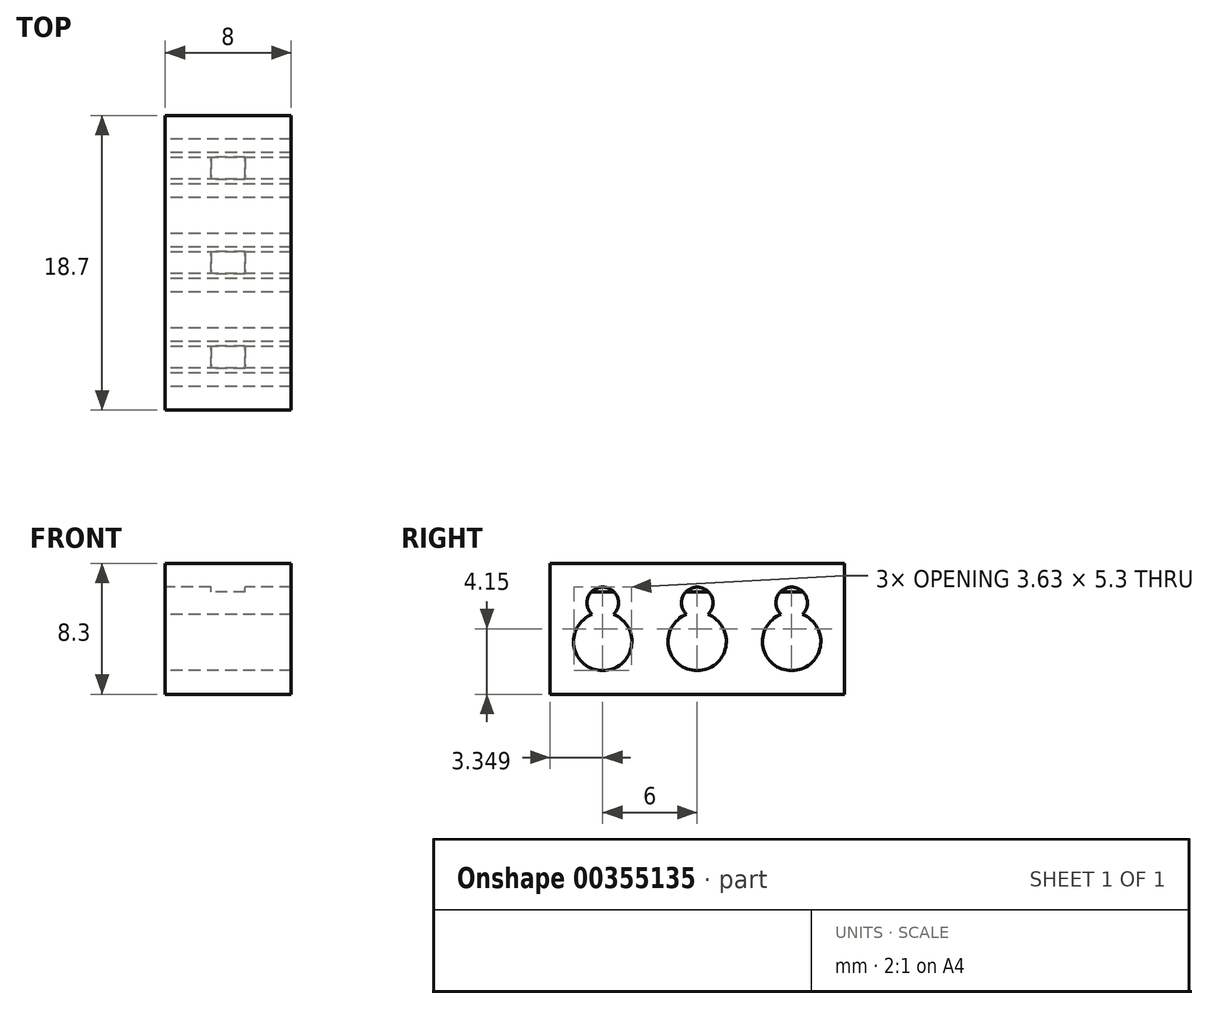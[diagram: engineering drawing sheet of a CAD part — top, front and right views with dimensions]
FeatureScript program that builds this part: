
annotation { "Feature Type Name" : "Feature", "Feature Type Description" : "" }
export const myFeature = defineFeature(function(context is Context, id is Id, definition is map)
    precondition{}
    {
        {
            var Q0;
            Q0=qCreatedBy(makeId("Right.planeOp"),FACE);
            var sketch = newSketch(context, id + "F0", { "sketchPlane" : qUnion([Q0])});
            skLineSegment(sketch, "E0.bottom", {"start": v(-6.61, -3.64) * mm, "end": v(12.09, -3.64) * mm});
            skLineSegment(sketch, "E0.top", {"start": v(-6.61, -11.94) * mm, "end": v(12.09, -11.94) * mm});
            skLineSegment(sketch, "E0.left", {"start": v(-6.61, -3.64) * mm, "end": v(-6.61, -11.94) * mm});
            skLineSegment(sketch, "E0.right", {"start": v(12.09, -3.64) * mm, "end": v(12.09, -11.94) * mm});
            skCircle(sketch, "E1", {"center": v(-3.26, -8.59) * mm, "radius": 1.85 * mm});
            skCircle(sketch, "E2", {"center": v(-3.26, -6.14) * mm, "radius": 1 * mm});
            skLineSegment(sketch, "E3", {"start": v(-3.26, -5.14) * mm, "end": v(-3.26, -10.44) * mm, "construction": true});
            skLineSegment(sketch, "E4.1.0.0", {"start": v(2.74, -5.14) * mm, "end": v(2.74, -10.44) * mm, "construction": true});
            skCircle(sketch, "E4.1.0.1", {"center": v(2.74, -8.59) * mm, "radius": 1.85 * mm});
            skCircle(sketch, "E4.1.0.2", {"center": v(2.74, -6.14) * mm, "radius": 1 * mm});
            skLineSegment(sketch, "E4.2.0.0", {"start": v(8.74, -5.14) * mm, "end": v(8.74, -10.44) * mm, "construction": true});
            skCircle(sketch, "E4.2.0.1", {"center": v(8.74, -8.59) * mm, "radius": 1.85 * mm});
            skCircle(sketch, "E4.2.0.2", {"center": v(8.74, -6.14) * mm, "radius": 1 * mm});
            skLineSegment(sketch, "E4.direction1", {"start": v(-3.26, -10.44) * mm, "end": v(2.74, -10.44) * mm, "construction": true});
            skSolve(sketch);
        }
        {
            var Q0;
            Q0=makeQuery(id+"F0.imprint","IMPRINT",FACE,{"disambiguationData":[TD([[makeQuery(id+"F0.imprint","IMPRINT",EDGE,{"derivedFrom":sQuery(id+"F0.wireOp",EDGE,"E0.bottom")}),-1.0]])]});
            extrude(context, id + "F1", {"entities" : qUnion([Q0]), "depth" : 8 * mm});
        }
        {
            var Q0;
            Q0=makeQuery(id+"F1.opExtrude","SWEPT_FACE",FACE,{"disambiguationData":[OSD([sQuery(id+"F0.wireOp",EDGE,"E0.bottom")])]});
            var sketch = newSketch(context, id + "F2", { "sketchPlane" : qUnion([Q0])});
            skLineSegment(sketch, "E5", {"start": v(0, 2.74) * mm, "end": v(8, 2.74) * mm, "construction": true});
            skLineSegment(sketch, "E6.bottom", {"start": v(5.09, 10.24) * mm, "end": v(2.91, 10.24) * mm});
            skLineSegment(sketch, "E6.top", {"start": v(5.09, -4.76) * mm, "end": v(2.91, -4.76) * mm});
            skLineSegment(sketch, "E6.left", {"start": v(5.09, 10.24) * mm, "end": v(5.09, -4.76) * mm});
            skLineSegment(sketch, "E6.right", {"start": v(2.91, 10.24) * mm, "end": v(2.91, -4.76) * mm});
            skPoint(sketch, "E6.middle", {"position": v(4, 2.74) * mm});
            skSolve(sketch);
        }
        {
            var Q0;
            Q0=makeQuery(id+"F2.imprint","IMPRINT",FACE,{"disambiguationData":[TD([[makeQuery(id+"F2.imprint","IMPRINT",EDGE,{"derivedFrom":sQuery(id+"F2.wireOp",EDGE,"E6.bottom")}),1.0]])]});
            extrude(context, id + "F3", {"entities" : qUnion([Q0]), "operationType" : NewBodyOperationType.ADD, "oppositeDirection" : true, "depth" : 1.8 * mm});
        }
    });
